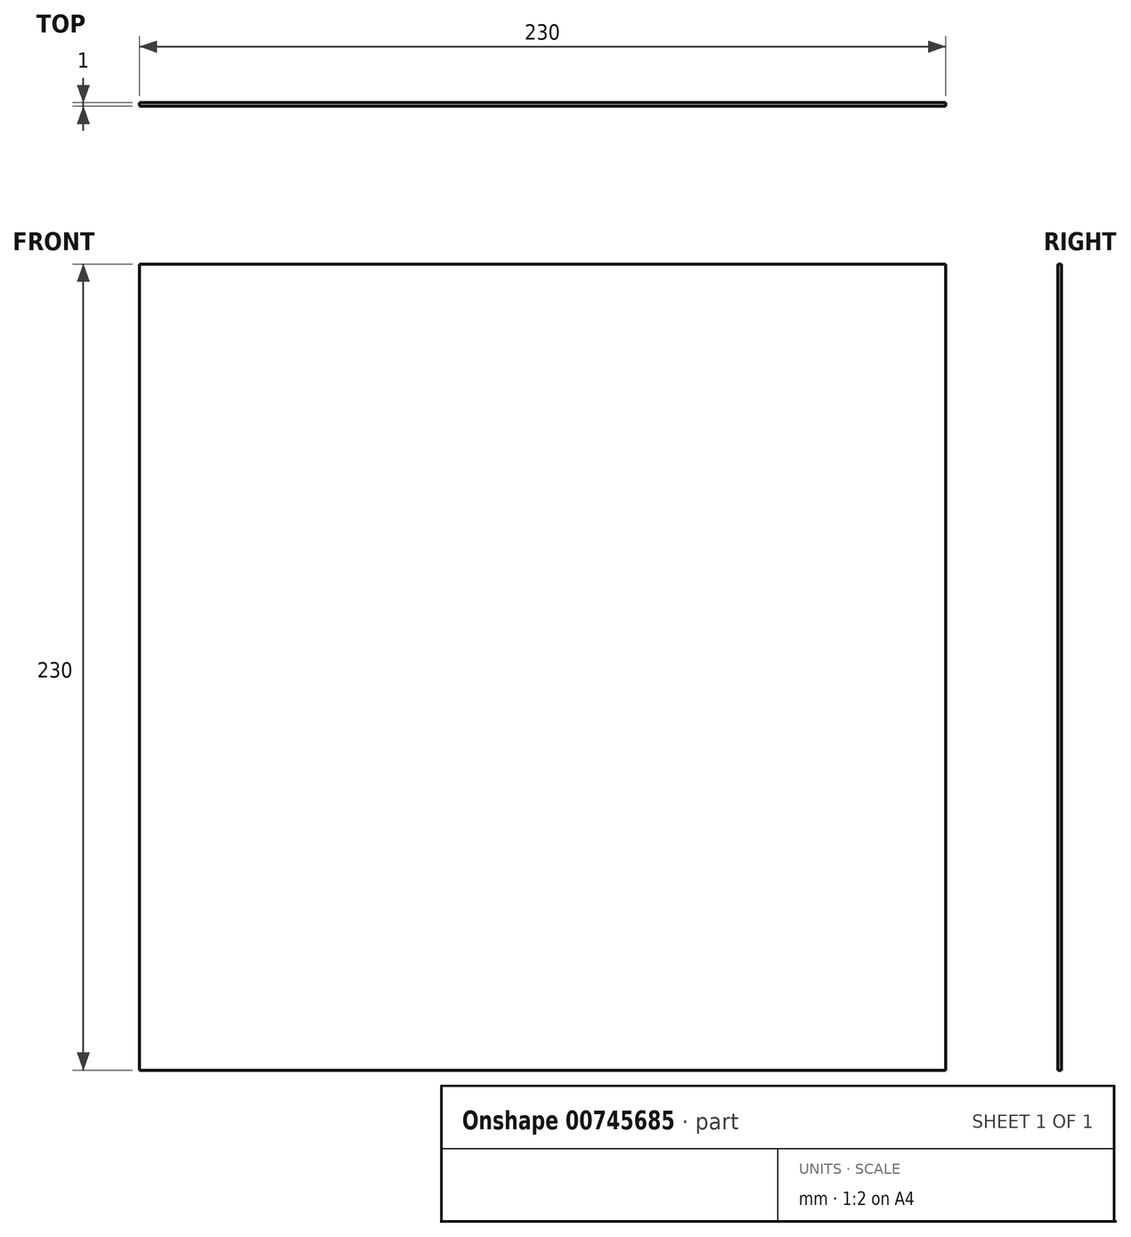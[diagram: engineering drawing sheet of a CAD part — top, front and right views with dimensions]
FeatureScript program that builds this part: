
annotation { "Feature Type Name" : "Feature", "Feature Type Description" : "" }
export const myFeature = defineFeature(function(context is Context, id is Id, definition is map)
    precondition{}
    {
        {
            var Q0;
            Q0=qCreatedBy(makeId("Front.planeOp"),FACE);
            var sketch = newSketch(context, id + "F0", { "sketchPlane" : qUnion([Q0])});
            skLineSegment(sketch, "E0.bottom", {"start": v(115, -115) * mm, "end": v(-115, -115) * mm});
            skLineSegment(sketch, "E0.top", {"start": v(115, 115) * mm, "end": v(-115, 115) * mm});
            skLineSegment(sketch, "E0.left", {"start": v(115, -115) * mm, "end": v(115, 115) * mm});
            skLineSegment(sketch, "E0.right", {"start": v(-115, -115) * mm, "end": v(-115, 115) * mm});
            skPoint(sketch, "E0.middle", {"position": v(0, 0) * mm});
            skSolve(sketch);
        }
        {
            var Q0;
            Q0 = qSketchRegion(id + "F0", true);
            extrude(context, id + "F1", {"entities" : qUnion([Q0]), "depth" : 1 * mm, "offsetDistance" : 25.4 * mm});
        }
    });
